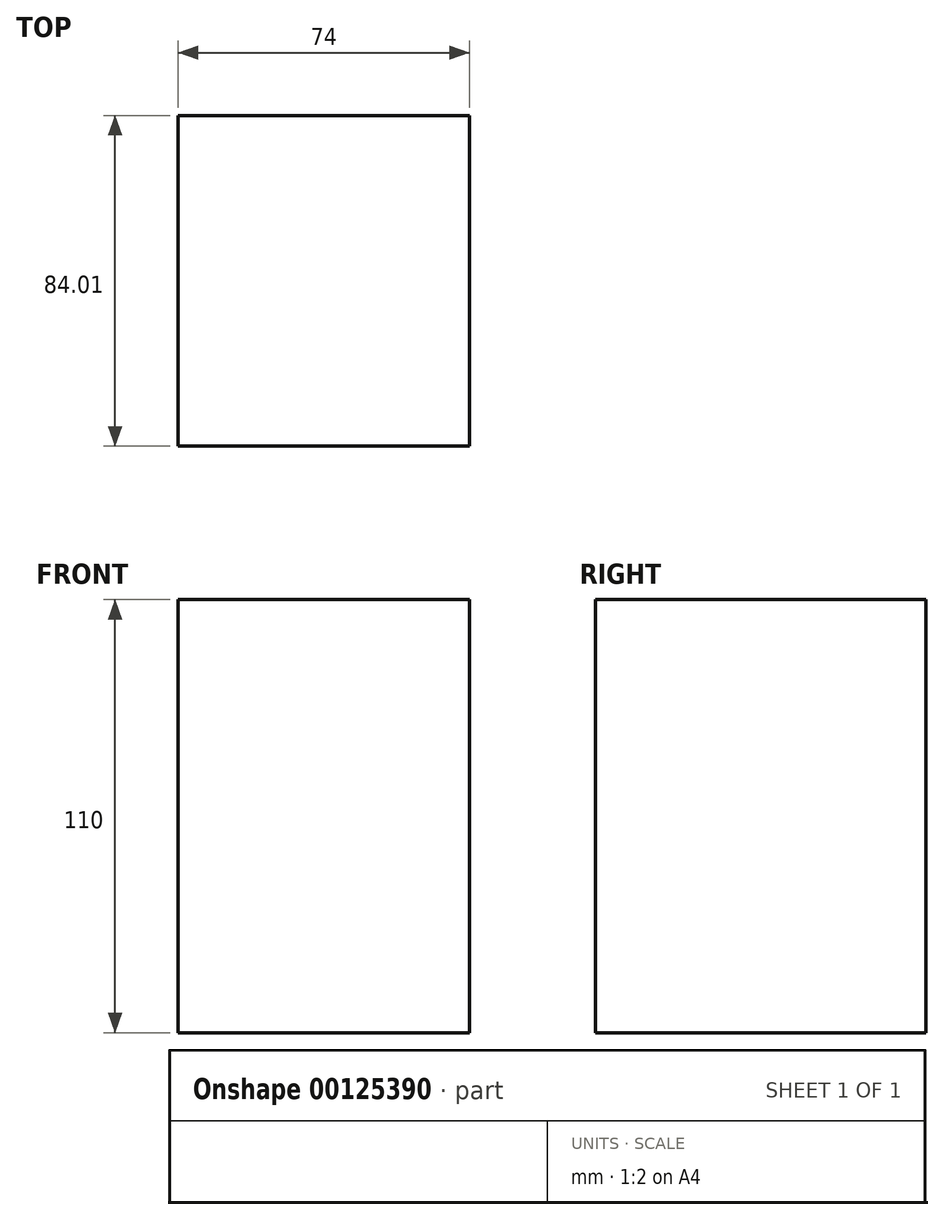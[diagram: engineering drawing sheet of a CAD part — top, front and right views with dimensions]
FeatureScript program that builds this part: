
annotation { "Feature Type Name" : "Feature", "Feature Type Description" : "" }
export const myFeature = defineFeature(function(context is Context, id is Id, definition is map)
    precondition{}
    {
        {
            var Q0;
            Q0=qCreatedBy(makeId("Front.planeOp"),FACE);
            var sketch = newSketch(context, id + "F0", { "sketchPlane" : qUnion([Q0])});
            skLineSegment(sketch, "E0.bottom", {"start": v(37, -55) * mm, "end": v(-37, -55) * mm});
            skLineSegment(sketch, "E0.top", {"start": v(37, 55) * mm, "end": v(-37, 55) * mm});
            skLineSegment(sketch, "E0.left", {"start": v(37, -55) * mm, "end": v(37, 55) * mm});
            skLineSegment(sketch, "E0.right", {"start": v(-37, -55) * mm, "end": v(-37, 55) * mm});
            skPoint(sketch, "E0.middle", {"position": v(0, 0) * mm});
            skSolve(sketch);
        }
        {
            var Q0;
            Q0=makeQuery(id+"F0.imprint","IMPRINT",FACE,{"disambiguationData":[TD([[makeQuery(id+"F0.imprint","IMPRINT",EDGE,{"derivedFrom":sQuery(id+"F0.wireOp",EDGE,"E0.bottom")}),-1.0]])]});
            extrude(context, id + "F1", {"entities" : qUnion([Q0]), "depth" : 84.01 * mm});
        }
    });
